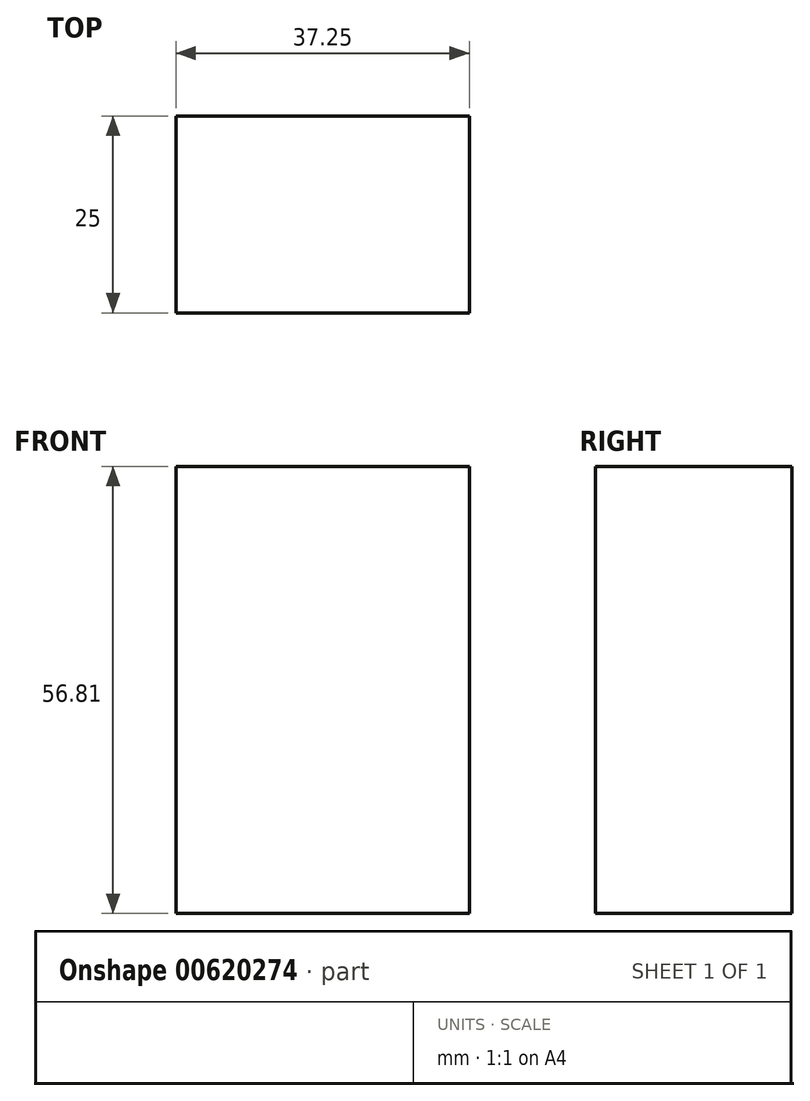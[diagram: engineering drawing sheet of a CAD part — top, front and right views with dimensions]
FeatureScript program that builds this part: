
annotation { "Feature Type Name" : "Feature", "Feature Type Description" : "" }
export const myFeature = defineFeature(function(context is Context, id is Id, definition is map)
    precondition{}
    {
        {
            var Q0;
            Q0=qCreatedBy(makeId("Front.planeOp"),FACE);
            var sketch = newSketch(context, id + "F0", { "sketchPlane" : qUnion([Q0])});
            skLineSegment(sketch, "E0.bottom", {"start": v(-8.88, 28.98) * mm, "end": v(28.37, 28.98) * mm});
            skLineSegment(sketch, "E0.top", {"start": v(-8.88, -27.83) * mm, "end": v(28.37, -27.83) * mm});
            skLineSegment(sketch, "E0.left", {"start": v(-8.88, 28.98) * mm, "end": v(-8.88, -27.83) * mm});
            skLineSegment(sketch, "E0.right", {"start": v(28.37, 28.98) * mm, "end": v(28.37, -27.83) * mm});
            skSolve(sketch);
        }
        {
            var Q0;
            Q0=makeQuery(id+"F0.imprint","IMPRINT",FACE,{"disambiguationData":[TD([[makeQuery(id+"F0.imprint","IMPRINT",EDGE,{"derivedFrom":sQuery(id+"F0.wireOp",EDGE,"E0.bottom")}),-1.0]])]});
            extrude(context, id + "F1", {"entities" : qUnion([Q0]), "depth" : 25 * mm, "offsetDistance" : 25 * mm});
        }
    });
